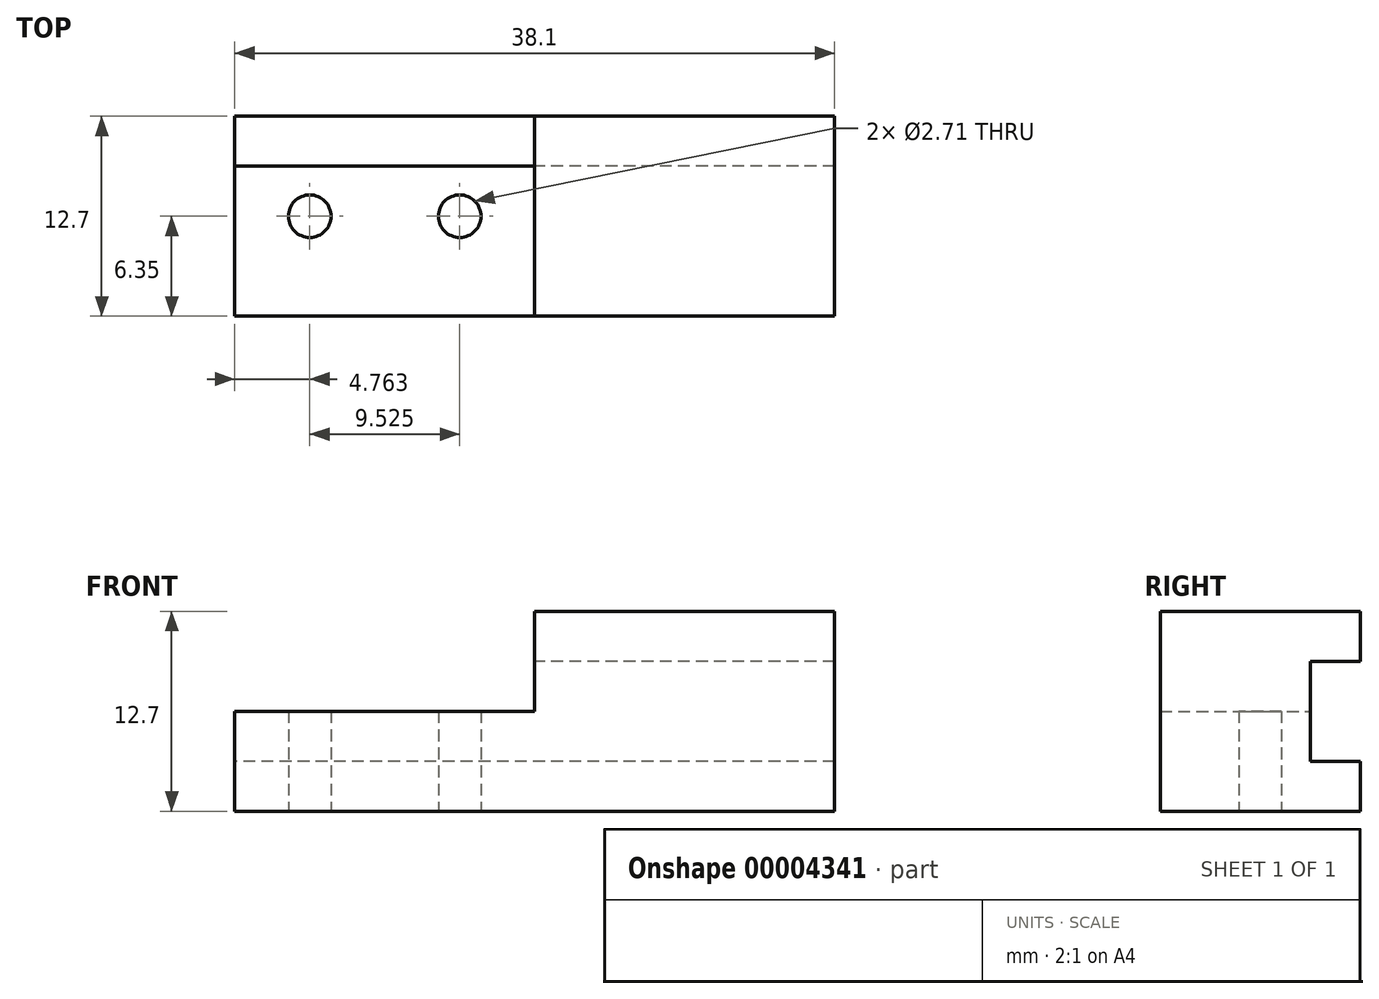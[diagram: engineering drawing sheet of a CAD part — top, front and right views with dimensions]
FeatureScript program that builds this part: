
annotation { "Feature Type Name" : "Feature", "Feature Type Description" : "" }
export const myFeature = defineFeature(function(context is Context, id is Id, definition is map)
    precondition{}
    {
        {
            var Q0;
            Q0=qCreatedBy(makeId("Front.planeOp"),FACE);
            var sketch = newSketch(context, id + "F0", { "sketchPlane" : qUnion([Q0])});
            skLineSegment(sketch, "E0", {"start": v(0, 6.35) * mm, "end": v(19.05, 6.35) * mm});
            skLineSegment(sketch, "E1", {"start": v(19.05, 6.35) * mm, "end": v(19.05, 12.7) * mm});
            skLineSegment(sketch, "E2", {"start": v(19.05, 12.7) * mm, "end": v(38.1, 12.7) * mm});
            skLineSegment(sketch, "E3", {"start": v(38.1, 12.7) * mm, "end": v(38.1, 0) * mm});
            skLineSegment(sketch, "E4", {"start": v(38.1, 0) * mm, "end": v(0, 0) * mm});
            skLineSegment(sketch, "E5", {"start": v(0, 0) * mm, "end": v(0, 6.35) * mm});
            skSolve(sketch);
        }
        {
            var Q0;
            Q0=makeQuery(id+"F0.imprint","IMPRINT",FACE,{"disambiguationData":[TD([[makeQuery(id+"F0.imprint","IMPRINT",EDGE,{"derivedFrom":sQuery(id+"F0.wireOp",EDGE,"E0")}),-1.0]])]});
            extrude(context, id + "F1", {"entities" : qUnion([Q0]), "depth" : 12.7 * mm, "symmetric" : true});
        }
        {
            var Q0;
            Q0=makeQuery(id+"F1.opExtrude","SWEPT_FACE",FACE,{"disambiguationData":[OSD([sQuery(id+"F0.wireOp",EDGE,"E0")])]});
            var sketch = newSketch(context, id + "F2", { "sketchPlane" : qUnion([Q0])});
            skPoint(sketch, "E6", {"position": v(4.76, 0) * mm});
            skPoint(sketch, "E7", {"position": v(14.29, 0) * mm});
            skLineSegment(sketch, "E8", {"start": v(0, 0) * mm, "end": v(4.76, 0) * mm, "construction": true});
            skLineSegment(sketch, "E9", {"start": v(14.29, 0) * mm, "end": v(19.05, 0) * mm, "construction": true});
            skSolve(sketch);
        }
        {
            var Q0;
            Q0=sQuery(id+"F2.wireOp",VERTEX,"E7");
            var Q1;
            Q1=sQuery(id+"F2.wireOp",VERTEX,"E6");
            var Q2;
            Q2=makeQuery(id+"F1.opExtrude","SWEPT_BODY",BODY,{"disambiguationData":[OSD([sQuery(id+"F0.wireOp",EDGE,"E0"),sQuery(id+"F0.wireOp",EDGE,"E1"),sQuery(id+"F0.wireOp",EDGE,"E2"),sQuery(id+"F0.wireOp",EDGE,"E3"),sQuery(id+"F0.wireOp",EDGE,"E4"),sQuery(id+"F0.wireOp",EDGE,"E5")])]});
            hole(context, id + "F3", {"style" : HoleStyle.SIMPLE, "holeDiameter" : 2.7 * mm, "endStyle" : HoleEndStyle.THROUGH, "locations" : qUnion([Q0, Q1]), "scope" : qUnion([Q2])});
        }
        {
            var Q0;
            Q0=makeQuery(id+"F1.opExtrude","CAP_FACE",FACE,{"disambiguationData":[OSD([sQuery(id+"F0.wireOp",EDGE,"E0"),sQuery(id+"F0.wireOp",EDGE,"E1"),sQuery(id+"F0.wireOp",EDGE,"E2"),sQuery(id+"F0.wireOp",EDGE,"E3"),sQuery(id+"F0.wireOp",EDGE,"E4"),sQuery(id+"F0.wireOp",EDGE,"E5")])],"isStart":true});
            var sketch = newSketch(context, id + "F4", { "sketchPlane" : qUnion([Q0])});
            skLineSegment(sketch, "E10.bottom", {"start": v(-38.1, 9.53) * mm, "end": v(0, 9.53) * mm});
            skLineSegment(sketch, "E10.top", {"start": v(-38.1, 3.18) * mm, "end": v(0, 3.18) * mm});
            skLineSegment(sketch, "E10.left", {"start": v(-38.1, 9.53) * mm, "end": v(-38.1, 3.18) * mm});
            skLineSegment(sketch, "E10.right", {"start": v(0, 9.53) * mm, "end": v(0, 3.18) * mm});
            skSolve(sketch);
        }
        {
            var Q0;
            {var subQ1=sQuery(id+"F4.wireOp",EDGE,"E10.top");Q0=makeQuery(id+"F4.imprint","IMPRINT",FACE,{"disambiguationData":[TD([[makeQuery(id+"F4.imprint","IMPRINT",EDGE,{"derivedFrom":subQ1}),1.0]])]});}
            extrude(context, id + "F5", {"entities" : qUnion([Q0]), "operationType" : NewBodyOperationType.REMOVE, "oppositeDirection" : true, "depth" : 3.17 * mm});
        }
    });
